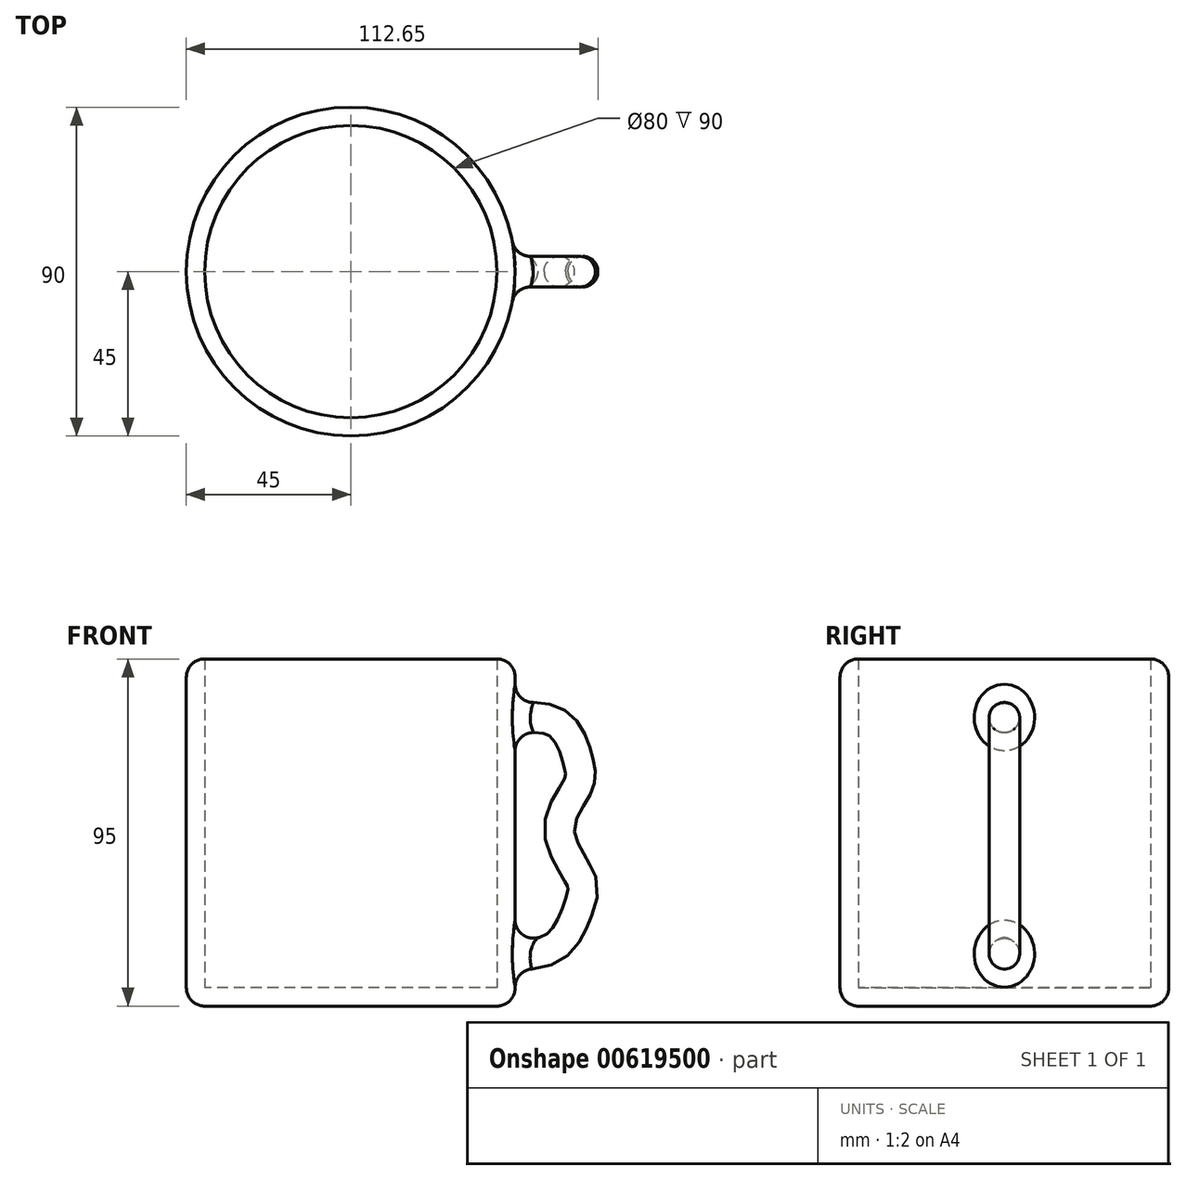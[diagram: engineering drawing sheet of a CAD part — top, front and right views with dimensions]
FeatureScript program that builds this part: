
annotation { "Feature Type Name" : "Feature", "Feature Type Description" : "" }
export const myFeature = defineFeature(function(context is Context, id is Id, definition is map)
    precondition{}
    {
        {
            var Q0;
            Q0=qCreatedBy(makeId("Top.planeOp"),FACE);
            var sketch = newSketch(context, id + "F0", { "sketchPlane" : qUnion([Q0])});
            skCircle(sketch, "E0", {"center": v(0, 0) * mm, "radius": 45 * mm});
            skSolve(sketch);
        }
        {
            var Q0;
            Q0=makeQuery(id+"F0.imprint","IMPRINT",FACE,{"disambiguationData":[TD([[makeQuery(id+"F0.imprint","IMPRINT",EDGE,{"derivedFrom":sQuery(id+"F0.wireOp",EDGE,"E0")}),1.0]])]});
            extrude(context, id + "F1", {"entities" : qUnion([Q0]), "depth" : 95 * mm, "offsetDistance" : 25 * mm});
        }
        {
            var Q0;
            Q0=qCreatedBy(makeId("Front.planeOp"),FACE);
            var sketch = newSketch(context, id + "F2", { "sketchPlane" : qUnion([Q0])});
            skFitSpline(sketch, "E1", {"points": [v(36.83, 77.65) * mm, v(56.94, 77.65) * mm, v(62.86, 66.4) * mm, v(62.56, 60.2) * mm, v(57.53, 48.36) * mm, v(63.45, 34.46) * mm, v(63.15, 27.95) * mm, v(56.35, 16.12) * mm, v(39.2, 14.05) * mm], "startDerivative": vector(148.06, 28.9) * mm, "endDerivative": vector(-132.88, 9.98) * mm});
            skSolve(sketch);
        }
        {
            var Q0;
            Q0=qCreatedBy(makeId("Right.planeOp"),FACE);
            cPlane(context, id + "F3", {"entities" : qUnion([Q0]), "cplaneType" : CPlaneType.OFFSET, "offset" : 41.9 * mm, "width" : 150 * mm, "height" : 150 * mm});
        }
        {
            var Q0;
            Q0=qCreatedBy(id+"F3.planeOp",FACE);
            var sketch = newSketch(context, id + "F4", { "sketchPlane" : qUnion([Q0])});
            skCircle(sketch, "E2", {"center": v(0, 78.14) * mm, "radius": 4.18 * mm});
            skSolve(sketch);
        }
        {
            var Q0;
            Q0 = qSketchRegion(id + "F4", true);
            var Q1;
            Q1=sQuery(id+"F2.wireOp",EDGE,"E1");
            sweep(context, id + "F5", {"operationType" : NewBodyOperationType.ADD, "profiles" : qUnion([Q0]), "path" : qUnion([Q1])});
        }
        {
            var Q0;
            Q0=makeQuery(id+"F1.opExtrude","CAP_FACE",FACE,{"disambiguationData":[OSD([sQuery(id+"F0.wireOp",EDGE,"E0")])],"isStart":false});
            shell(context, id + "F6", {"entities" : qUnion([Q0]), "thickness" : 5 * mm});
        }
        {
            var Q0;
            Q0=makeQuery(id+"F1.opExtrude","SWEPT_FACE",FACE,{"disambiguationData":[OSD([sQuery(id+"F0.wireOp",EDGE,"E0")])]});
            fillet(context, id + "F7", {"entities" : qUnion([Q0]), "radius" : 5 * mm, "tangentPropagation" : true, "allowEdgeOverflow" : false});
        }
    });
